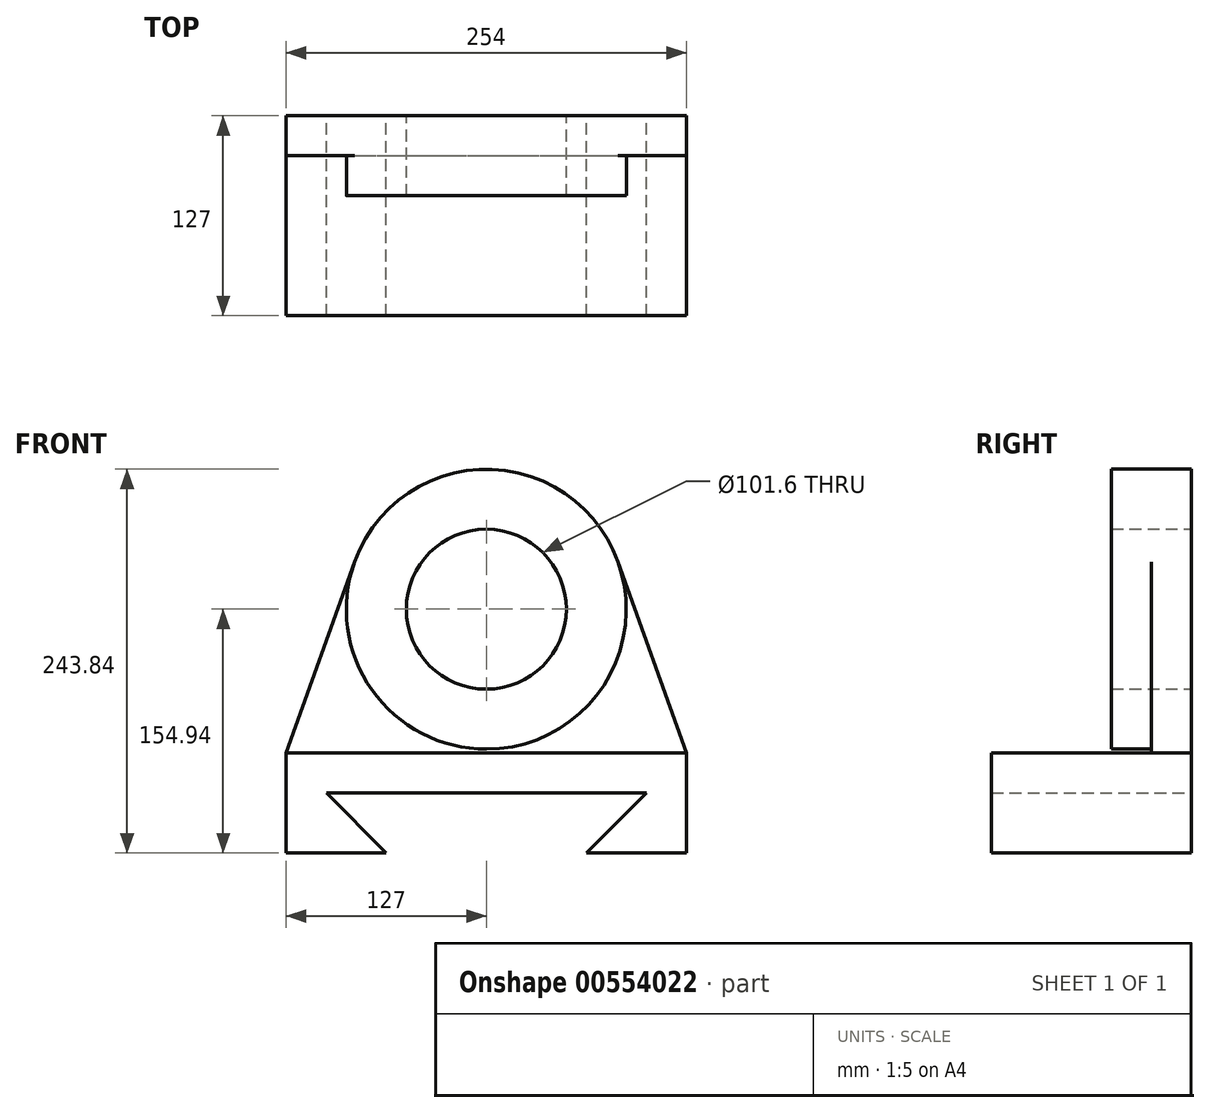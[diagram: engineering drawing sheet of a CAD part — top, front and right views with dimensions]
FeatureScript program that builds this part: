
annotation { "Feature Type Name" : "Feature", "Feature Type Description" : "" }
export const myFeature = defineFeature(function(context is Context, id is Id, definition is map)
    precondition{}
    {
        {
            var Q0;
            Q0=qCreatedBy(makeId("Front.planeOp"),FACE);
            var sketch = newSketch(context, id + "F0", { "sketchPlane" : qUnion([Q0])});
            skCircle(sketch, "E0", {"center": v(0, 0) * mm, "radius": 88.9 * mm});
            skCircle(sketch, "E1", {"center": v(0, 0) * mm, "radius": 50.8 * mm});
            skLineSegment(sketch, "E2", {"start": v(-83.73, 29.87) * mm, "end": v(-127, -91.44) * mm});
            skLineSegment(sketch, "E3", {"start": v(-127, -91.44) * mm, "end": v(-127, -154.94) * mm});
            skLineSegment(sketch, "E4", {"start": v(-127, -91.44) * mm, "end": v(127, -91.44) * mm});
            skLineSegment(sketch, "E5", {"start": v(83.73, 29.87) * mm, "end": v(127, -91.44) * mm});
            skLineSegment(sketch, "E6", {"start": v(127, -91.44) * mm, "end": v(127, -154.94) * mm});
            skLineSegment(sketch, "E7", {"start": v(-63.5, -154.94) * mm, "end": v(-101.6, -116.84) * mm});
            skLineSegment(sketch, "E8", {"start": v(-101.6, -116.84) * mm, "end": v(101.6, -116.84) * mm});
            skLineSegment(sketch, "E9", {"start": v(101.6, -116.84) * mm, "end": v(63.5, -154.94) * mm});
            skLineSegment(sketch, "E10", {"start": v(63.5, -154.94) * mm, "end": v(127, -154.94) * mm});
            skLineSegment(sketch, "E11", {"start": v(-63.5, -154.94) * mm, "end": v(-127, -154.94) * mm});
            skSolve(sketch);
        }
        {
            var Q0;
            Q0=makeQuery(id+"F0.imprint","IMPRINT",FACE,{"disambiguationData":[TD([[makeQuery(id+"F0.imprint","IMPRINT",EDGE,{"derivedFrom":sQuery(id+"F0.wireOp",EDGE,"E3")}),1.0]])]});
            extrude(context, id + "F1", {"entities" : qUnion([Q0]), "depth" : 127 * mm, "offsetDistance" : 25.4 * mm});
        }
        {
            var Q0;
            {var subQ0=sQuery(id+"F0.wireOp",EDGE,"E2");Q0=makeQuery(id+"F0.imprint","IMPRINT",FACE,{"disambiguationData":[TD([[makeQuery(id+"F0.imprint","IMPRINT",EDGE,{"derivedFrom":subQ0}),1.0]])]});}
            extrude(context, id + "F2", {"entities" : qUnion([Q0]), "operationType" : NewBodyOperationType.ADD, "depth" : 25.4 * mm, "offsetDistance" : 25.4 * mm});
        }
        {
            var Q0;
            Q0=makeQuery(id+"F0.imprint","IMPRINT",FACE,{"disambiguationData":[TD([[makeQuery(id+"F0.imprint","IMPRINT",EDGE,{"derivedFrom":sQuery(id+"F0.wireOp",EDGE,"E1")}),-1.0]])]});
            extrude(context, id + "F3", {"entities" : qUnion([Q0]), "operationType" : NewBodyOperationType.ADD, "depth" : 50.8 * mm, "offsetDistance" : 25.4 * mm});
        }
    });
